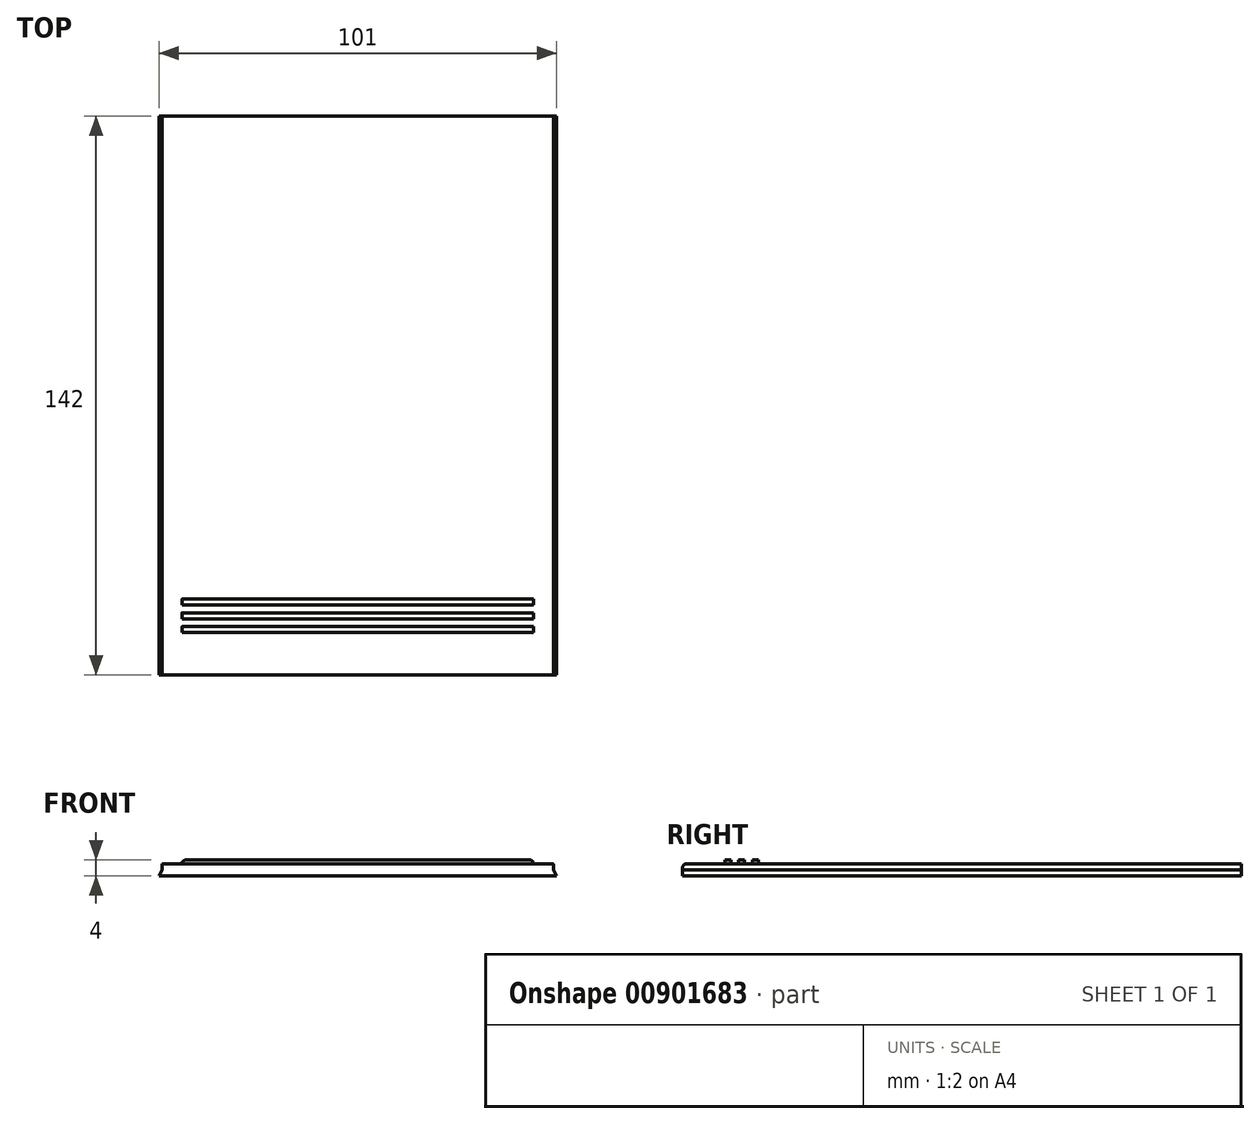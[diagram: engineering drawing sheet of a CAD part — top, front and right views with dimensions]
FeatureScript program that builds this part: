
annotation { "Feature Type Name" : "Feature", "Feature Type Description" : "" }
export const myFeature = defineFeature(function(context is Context, id is Id, definition is map)
    precondition{}
    {
        {
            var Q0;
            Q0=qCreatedBy(makeId("Front.planeOp"),FACE);
            var sketch = newSketch(context, id + "F0", { "sketchPlane" : qUnion([Q0])});
            skLineSegment(sketch, "E0.bottom", {"start": v(0, 0) * mm, "end": v(49.7, 0) * mm});
            skLineSegment(sketch, "E0.top", {"start": v(0, -1.5) * mm, "end": v(49.7, -1.5) * mm});
            skLineSegment(sketch, "E0.left", {"start": v(0, 0) * mm, "end": v(0, -1.5) * mm});
            skLineSegment(sketch, "E0.right", {"start": v(49.7, 0) * mm, "end": v(49.7, -1.5) * mm});
            skLineSegment(sketch, "E1", {"start": v(0, -1.5) * mm, "end": v(0, -3) * mm});
            skLineSegment(sketch, "E2", {"start": v(0, -3) * mm, "end": v(50.5, -3) * mm});
            skLineSegment(sketch, "E3", {"start": v(50.5, -3) * mm, "end": v(49.7, -1.5) * mm});
            skLineSegment(sketch, "E4.MirrorCS", {"start": v(-49.7, 0) * mm, "end": v(-49.7, -1.5) * mm});
            skLineSegment(sketch, "E5.MirrorCS", {"start": v(-50.5, -3) * mm, "end": v(-49.7, -1.5) * mm});
            skLineSegment(sketch, "E6.MirrorCS", {"start": v(0, -3) * mm, "end": v(-50.5, -3) * mm});
            skLineSegment(sketch, "E7.MirrorCS", {"start": v(0, 0) * mm, "end": v(-49.7, 0) * mm});
            skLineSegment(sketch, "E8.MirrorCS", {"start": v(0, -1.5) * mm, "end": v(-49.7, -1.5) * mm});
            skSolve(sketch);
        }
        {
            var Q0;
            Q0 = qSketchRegion(id + "F0", true);
            extrude(context, id + "F1", {"entities" : qUnion([Q0]), "depth" : 142 * mm, "offsetDistance" : 25 * mm});
        }
        {
            var Q0;
            Q0=makeQuery(id+"F1.opExtrude","SWEPT_FACE",FACE,{"disambiguationData":[OSD([sQuery(id+"F0.wireOp",EDGE,"E0.bottom"),sQuery(id+"F0.wireOp",EDGE,"E7.MirrorCS")])]});
            var sketch = newSketch(context, id + "F2", { "sketchPlane" : qUnion([Q0])});
            skLineSegment(sketch, "E9.bottom", {"start": v(-44.69, -131.21) * mm, "end": v(0, -131.21) * mm});
            skLineSegment(sketch, "E9.top", {"start": v(-44.69, -129.71) * mm, "end": v(0, -129.71) * mm});
            skLineSegment(sketch, "E9.left", {"start": v(-44.69, -131.21) * mm, "end": v(-44.69, -129.71) * mm});
            skLineSegment(sketch, "E9.right", {"start": v(0, -131.21) * mm, "end": v(0, -129.71) * mm});
            skLineSegment(sketch, "E10.bottom", {"start": v(-44.69, -127.71) * mm, "end": v(0, -127.71) * mm});
            skLineSegment(sketch, "E10.top", {"start": v(-44.69, -126.21) * mm, "end": v(0, -126.21) * mm});
            skLineSegment(sketch, "E10.left", {"start": v(-44.69, -127.71) * mm, "end": v(-44.69, -126.21) * mm});
            skLineSegment(sketch, "E10.right", {"start": v(0, -127.71) * mm, "end": v(0, -126.21) * mm});
            skLineSegment(sketch, "E11.bottom", {"start": v(-44.69, -124.21) * mm, "end": v(0, -124.21) * mm});
            skLineSegment(sketch, "E11.top", {"start": v(-44.69, -122.71) * mm, "end": v(0, -122.71) * mm});
            skLineSegment(sketch, "E11.left", {"start": v(-44.69, -124.21) * mm, "end": v(-44.69, -122.71) * mm});
            skLineSegment(sketch, "E11.right", {"start": v(0, -124.21) * mm, "end": v(0, -122.71) * mm});
            skLineSegment(sketch, "E12.MirrorCS", {"start": v(44.69, -124.21) * mm, "end": v(44.69, -122.71) * mm});
            skLineSegment(sketch, "E13.MirrorCS", {"start": v(44.69, -127.71) * mm, "end": v(44.69, -126.21) * mm});
            skLineSegment(sketch, "E14.MirrorCS", {"start": v(44.69, -131.21) * mm, "end": v(44.69, -129.71) * mm});
            skLineSegment(sketch, "E15.MirrorCS", {"start": v(44.69, -122.71) * mm, "end": v(0, -122.71) * mm});
            skLineSegment(sketch, "E16.MirrorCS", {"start": v(44.69, -126.21) * mm, "end": v(0, -126.21) * mm});
            skLineSegment(sketch, "E17.MirrorCS", {"start": v(44.69, -131.21) * mm, "end": v(0, -131.21) * mm});
            skLineSegment(sketch, "E18.MirrorCS", {"start": v(44.69, -129.71) * mm, "end": v(0, -129.71) * mm});
            skLineSegment(sketch, "E19.MirrorCS", {"start": v(44.69, -127.71) * mm, "end": v(0, -127.71) * mm});
            skLineSegment(sketch, "E20.MirrorCS", {"start": v(44.69, -124.21) * mm, "end": v(0, -124.21) * mm});
            skSolve(sketch);
        }
        {
            var Q0;
            Q0 = qSketchRegion(id + "F2", true);
            extrude(context, id + "F3", {"entities" : qUnion([Q0]), "operationType" : NewBodyOperationType.ADD, "depth" : 1 * mm, "offsetDistance" : 25 * mm});
        }
        {
            var Q0;
            Q0=makeQuery(id+"F3.opExtrude","CAP_EDGE",EDGE,{"disambiguationData":[OSD([sQuery(id+"F2.wireOp",EDGE,"E11.left")])],"isStart":false});
            var Q1;
            Q1=makeQuery(id+"F3.opExtrude","CAP_EDGE",EDGE,{"disambiguationData":[OSD([sQuery(id+"F2.wireOp",EDGE,"E10.left")])],"isStart":false});
            var Q2;
            Q2=makeQuery(id+"F3.opExtrude","CAP_EDGE",EDGE,{"disambiguationData":[OSD([sQuery(id+"F2.wireOp",EDGE,"E9.left")])],"isStart":false});
            var Q3;
            Q3=makeQuery(id+"F3.opExtrude","CAP_EDGE",EDGE,{"disambiguationData":[OSD([sQuery(id+"F2.wireOp",EDGE,"E12.MirrorCS")])],"isStart":false});
            var Q4;
            Q4=makeQuery(id+"F3.opExtrude","CAP_EDGE",EDGE,{"disambiguationData":[OSD([sQuery(id+"F2.wireOp",EDGE,"E13.MirrorCS")])],"isStart":false});
            var Q5;
            Q5=makeQuery(id+"F3.opExtrude","CAP_EDGE",EDGE,{"disambiguationData":[OSD([sQuery(id+"F2.wireOp",EDGE,"E14.MirrorCS")])],"isStart":false});
            var Q6;
            Q6=makeQuery(id+"F1.opExtrude","CAP_EDGE",EDGE,{"disambiguationData":[OSD([sQuery(id+"F0.wireOp",EDGE,"E0.bottom"),sQuery(id+"F0.wireOp",EDGE,"E7.MirrorCS")])],"isStart":false});
            fillet(context, id + "F4", {"entities" : qUnion([Q0, Q1, Q2, Q3, Q4, Q5, Q6]), "radius" : 1 * mm, "tangentPropagation" : true, "allowEdgeOverflow" : false});
        }
    });
